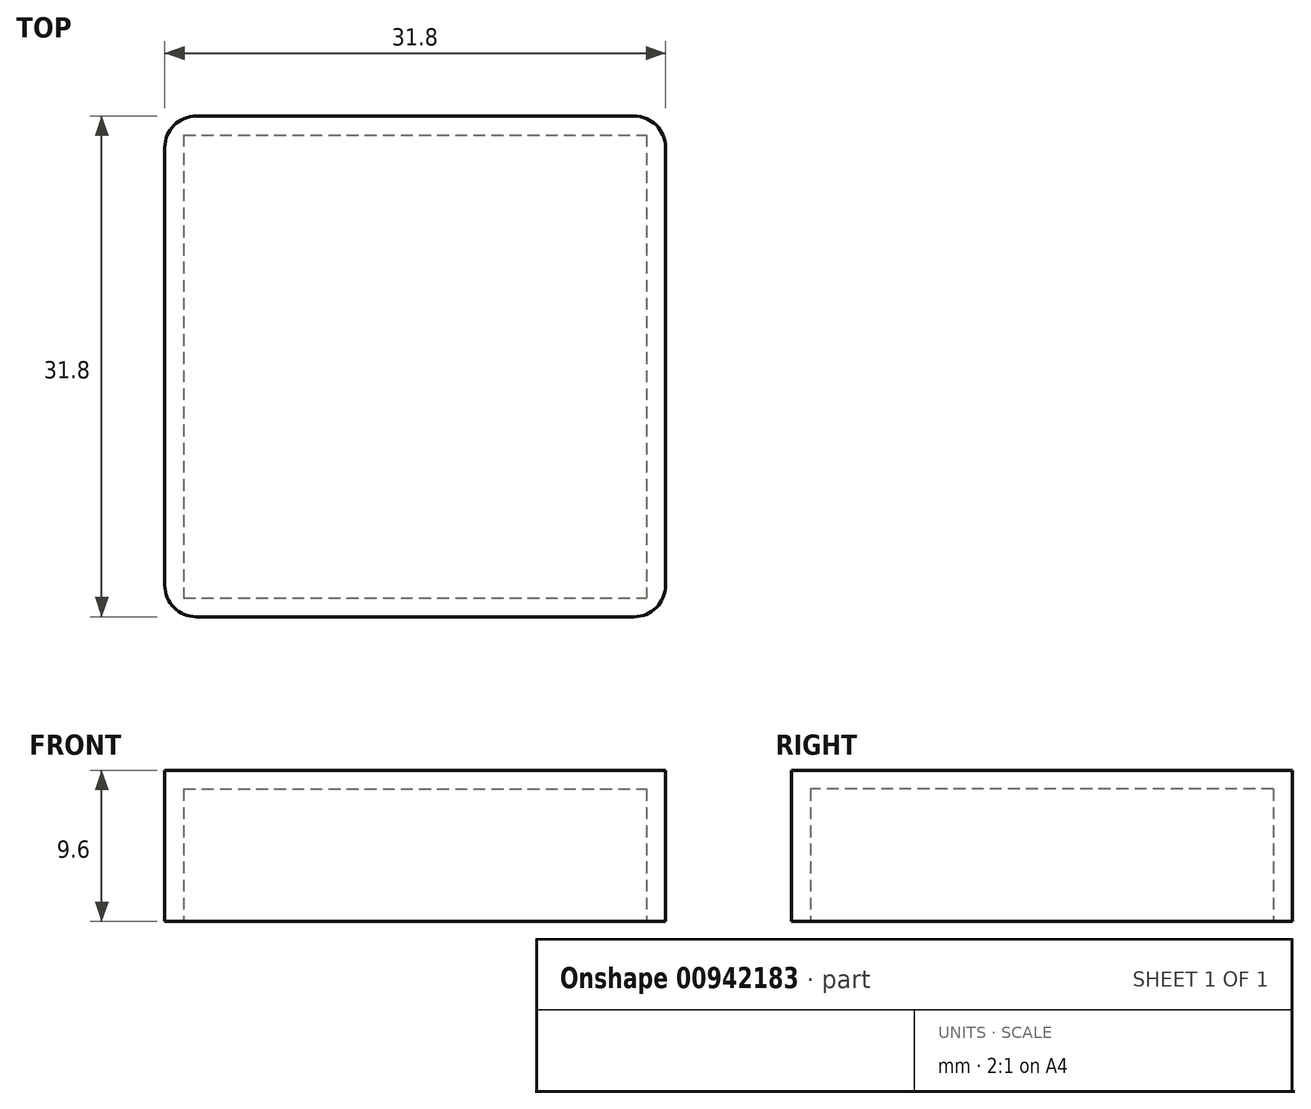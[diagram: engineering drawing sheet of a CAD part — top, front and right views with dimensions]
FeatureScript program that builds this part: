
annotation { "Feature Type Name" : "Feature", "Feature Type Description" : "" }
export const myFeature = defineFeature(function(context is Context, id is Id, definition is map)
    precondition{}
    {
        {
            var Q0;
            Q0=qCreatedBy(makeId("Top.planeOp"),FACE);
            var sketch = newSketch(context, id + "F0", { "sketchPlane" : qUnion([Q0])});
            skLineSegment(sketch, "E0.bottom", {"start": v(-15.9, 15.9) * mm, "end": v(15.9, 15.9) * mm});
            skLineSegment(sketch, "E0.top", {"start": v(-15.9, -15.9) * mm, "end": v(15.9, -15.9) * mm});
            skLineSegment(sketch, "E0.left", {"start": v(-15.9, 15.9) * mm, "end": v(-15.9, -15.9) * mm});
            skLineSegment(sketch, "E0.right", {"start": v(15.9, 15.9) * mm, "end": v(15.9, -15.9) * mm});
            skSolve(sketch);
        }
        {
            var Q0;
            Q0 = qSketchRegion(id + "F0", true);
            var Q1;
            Q1 = qSketchRegion(id + "F2", true);
            extrude(context, id + "F1", {"entities" : qUnion([Q0, Q1]), "depth" : 9.6 * mm, "offsetDistance" : 25 * mm});
        }
        {
            var Q0;
            Q0=qCreatedBy(makeId("Top.planeOp"),FACE);
            var sketch = newSketch(context, id + "F2", { "sketchPlane" : qUnion([Q0])});
            skLineSegment(sketch, "E1.bottom", {"start": v(-14.7, 14.7) * mm, "end": v(14.7, 14.7) * mm});
            skLineSegment(sketch, "E1.top", {"start": v(-14.7, -14.7) * mm, "end": v(14.7, -14.7) * mm});
            skLineSegment(sketch, "E1.left", {"start": v(-14.7, 14.7) * mm, "end": v(-14.7, -14.7) * mm});
            skLineSegment(sketch, "E1.right", {"start": v(14.7, 14.7) * mm, "end": v(14.7, -14.7) * mm});
            skSolve(sketch);
        }
        {
            var Q0;
            Q0 = qSketchRegion(id + "F2", true);
            extrude(context, id + "F3", {"entities" : qUnion([Q0]), "operationType" : NewBodyOperationType.REMOVE, "depth" : 8.4 * mm, "offsetDistance" : 25 * mm});
        }
        {
            var Q0;
            Q0=makeQuery(id+"F1.opExtrude","SWEPT_EDGE",EDGE,{"disambiguationData":[OSD([sQuery(id+"F0.wireOp",EDGE,"E0.top"),sQuery(id+"F0.wireOp",EDGE,"E0.left")])]});
            var Q1;
            Q1=makeQuery(id+"F1.opExtrude","SWEPT_EDGE",EDGE,{"disambiguationData":[OSD([sQuery(id+"F0.wireOp",EDGE,"E0.bottom"),sQuery(id+"F0.wireOp",EDGE,"E0.left")])]});
            var Q2;
            Q2=makeQuery(id+"F1.opExtrude","SWEPT_EDGE",EDGE,{"disambiguationData":[OSD([sQuery(id+"F0.wireOp",EDGE,"E0.bottom"),sQuery(id+"F0.wireOp",EDGE,"E0.right")])]});
            var Q3;
            Q3=makeQuery(id+"F1.opExtrude","SWEPT_EDGE",EDGE,{"disambiguationData":[OSD([sQuery(id+"F0.wireOp",EDGE,"E0.top"),sQuery(id+"F0.wireOp",EDGE,"E0.right")])]});
            fillet(context, id + "F4", {"entities" : qUnion([Q0, Q1, Q2, Q3]), "radius" : 2 * mm, "tangentPropagation" : true, "allowEdgeOverflow" : false});
        }
    });
